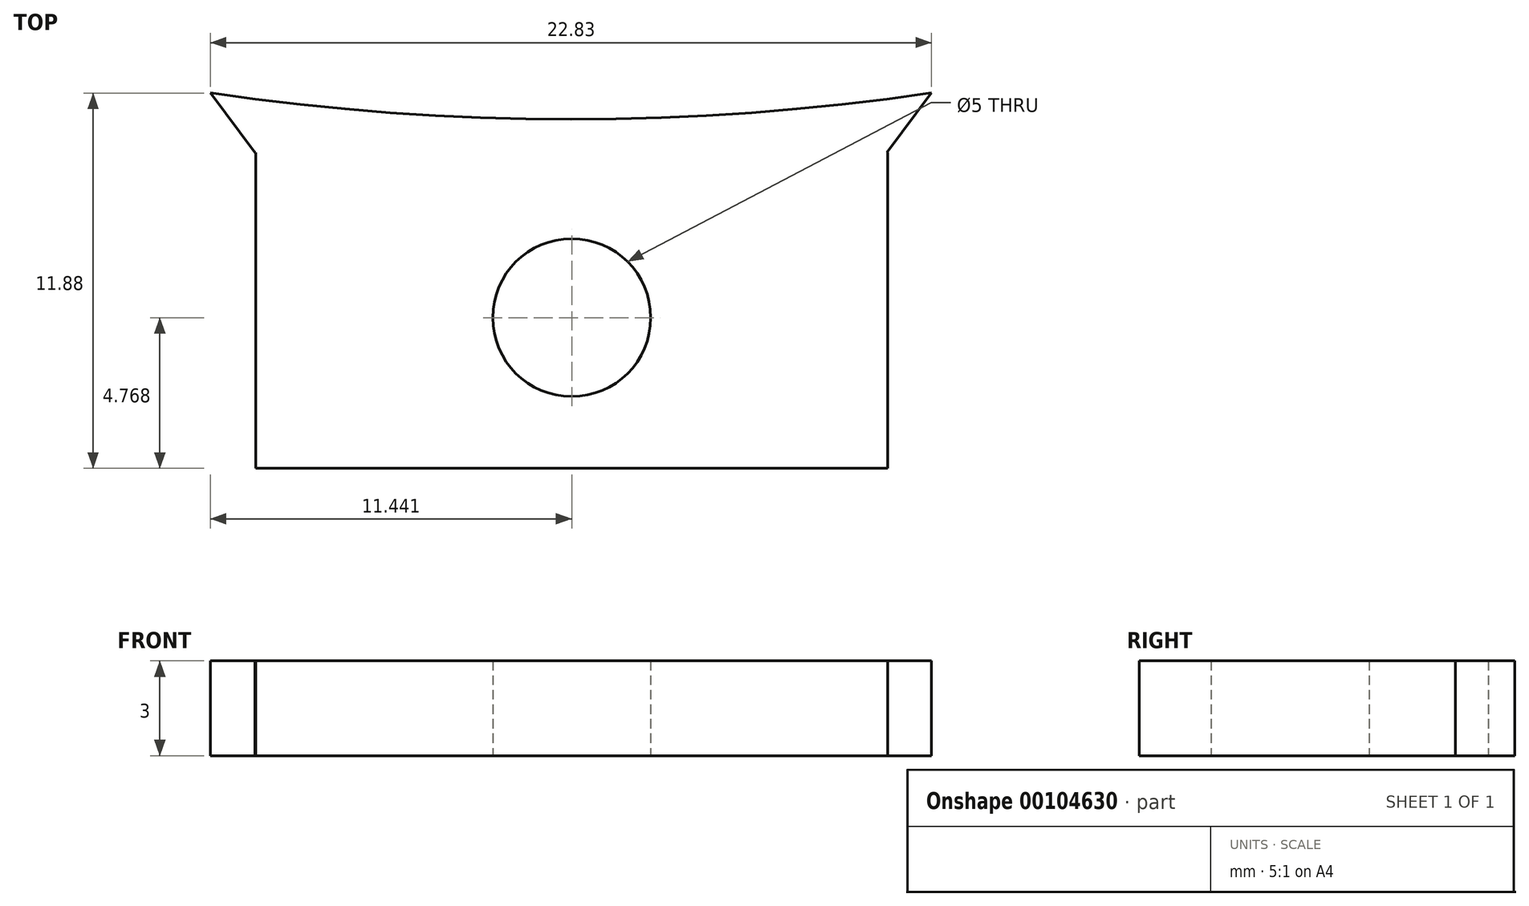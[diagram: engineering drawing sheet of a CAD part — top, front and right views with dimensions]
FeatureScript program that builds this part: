
annotation { "Feature Type Name" : "Feature", "Feature Type Description" : "" }
export const myFeature = defineFeature(function(context is Context, id is Id, definition is map)
    precondition{}
    {
        {
            var Q0;
            Q0=qCreatedBy(makeId("Top.planeOp"),FACE);
            var sketch = newSketch(context, id + "F0", { "sketchPlane" : qUnion([Q0])});
            skLineSegment(sketch, "E0.bottom", {"start": v(-14.86, 9) * mm, "end": v(5.14, 9) * mm});
            skLineSegment(sketch, "E0.top", {"start": v(-14.86, -1) * mm, "end": v(5.14, -1) * mm});
            skLineSegment(sketch, "E0.left", {"start": v(-14.86, 9) * mm, "end": v(-14.86, -1) * mm});
            skLineSegment(sketch, "E0.right", {"start": v(5.14, 9) * mm, "end": v(5.14, -1) * mm});
            skLineSegment(sketch, "E1.bottom", {"start": v(-14.88, 9) * mm, "end": v(5.12, 9) * mm});
            skLineSegment(sketch, "E1.top", {"start": v(-16.38, 11) * mm, "end": v(6.62, 11) * mm});
            skLineSegment(sketch, "E1.left", {"start": v(-14.88, 9) * mm, "end": v(-16.38, 11) * mm});
            skLineSegment(sketch, "E1.right", {"start": v(5.12, 9) * mm, "end": v(6.62, 11) * mm});
            skCircle(sketch, "E2", {"center": v(-4.88, 88.34) * mm, "radius": 78.28 * mm});
            skCircle(sketch, "E3", {"center": v(-4.86, 3.78) * mm, "radius": 2.5 * mm});
            skSolve(sketch);
        }
        {
            var Q0;
            {var subQ1=sQuery(id+"F0.wireOp",EDGE,"E1.bottom");var subQ8=makeQuery(id+"F0.imprint","INTERSECT",VERTEX,{"derivedFrom":[sQuery(id+"F0.wireOp",EDGE,"E0.right"),subQ1]});Q0=makeQuery(id+"F0.imprint","IMPRINT",FACE,{"disambiguationData":[TD([[makeQuery(id+"F0.imprint","IMPRINT",EDGE,{"disambiguationData":[TD([[subQ8,-1.0]])],"derivedFrom":subQ1}),1.0]])]});}
            var Q1;
            {var subQ1=sQuery(id+"F0.wireOp",EDGE,"E0.bottom");Q1=makeQuery(id+"F0.imprint","IMPRINT",FACE,{"disambiguationData":[TD([[makeQuery(id+"F0.imprint","IMPRINT",EDGE,{"derivedFrom":subQ1}),-1.0]])]});}
            extrude(context, id + "F1", {"entities" : qUnion([Q0, Q1]), "depth" : 3 * mm});
        }
    });
